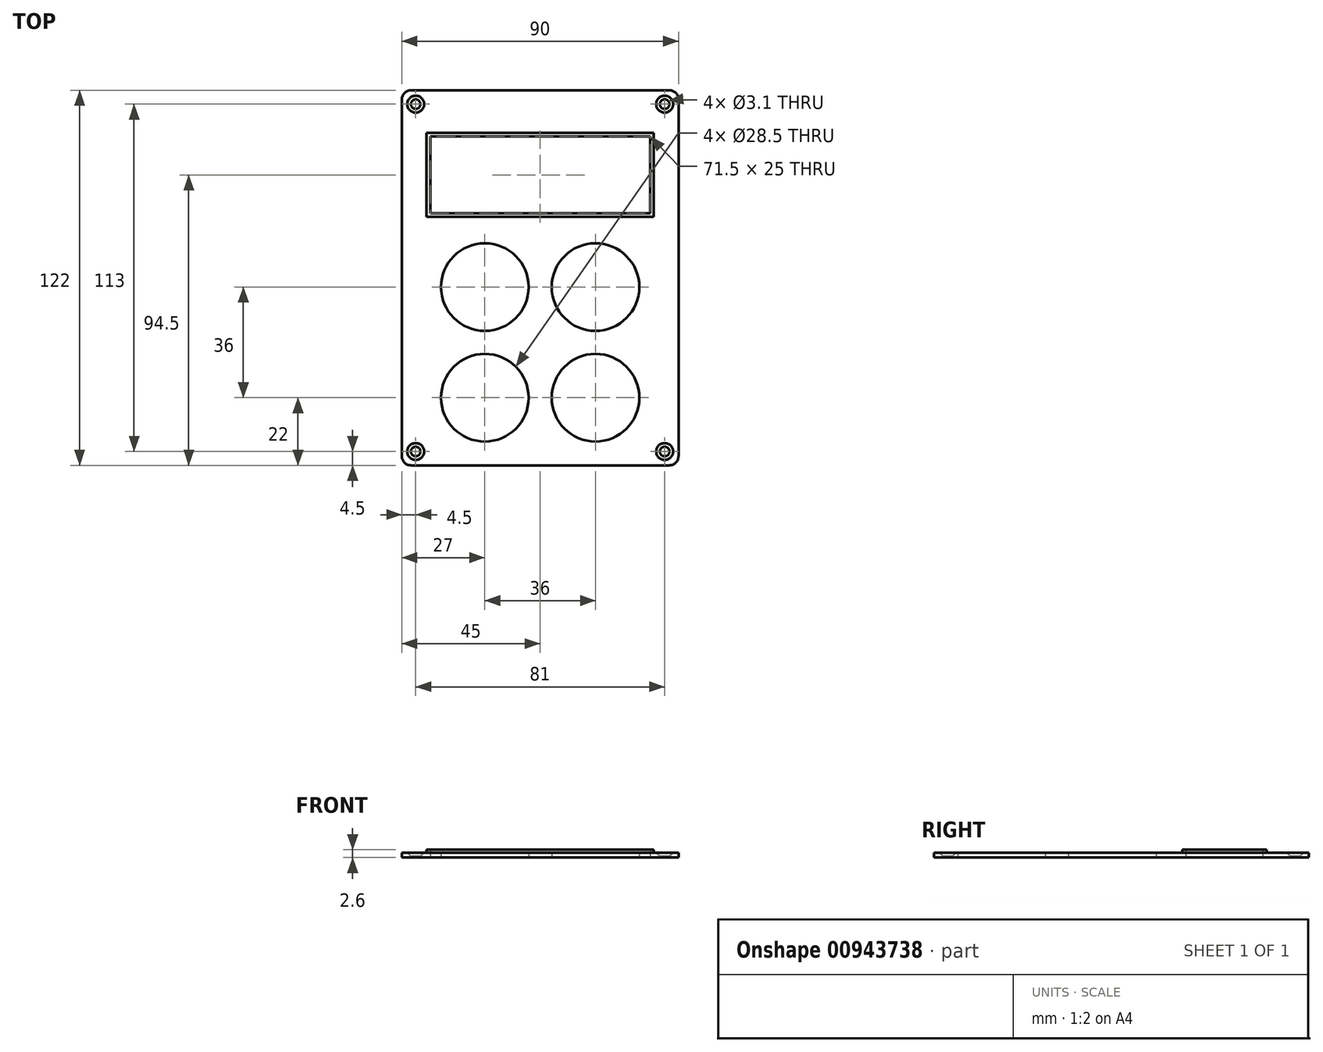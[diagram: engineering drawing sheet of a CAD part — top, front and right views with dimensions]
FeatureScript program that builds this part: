
annotation { "Feature Type Name" : "Feature", "Feature Type Description" : "" }
export const myFeature = defineFeature(function(context is Context, id is Id, definition is map)
    precondition{}
    {
        {
            var Q0;
            Q0=qCreatedBy(makeId("Top.planeOp"),FACE);
            var sketch = newSketch(context, id + "F0", { "sketchPlane" : qUnion([Q0])});
            skLineSegment(sketch, "E0.bottom", {"start": v(42, -94.5) * mm, "end": v(-42, -94.5) * mm});
            skLineSegment(sketch, "E0.top", {"start": v(42, 27.5) * mm, "end": v(-42, 27.5) * mm});
            skLineSegment(sketch, "E0.left", {"start": v(45, -91.5) * mm, "end": v(45, 24.5) * mm});
            skLineSegment(sketch, "E0.right", {"start": v(-45, -91.5) * mm, "end": v(-45, 24.5) * mm});
            skCircle(sketch, "E1", {"center": v(-40.5, -90) * mm, "radius": 1.55 * mm});
            skCircle(sketch, "E2", {"center": v(40.5, 23) * mm, "radius": 1.55 * mm});
            skCircle(sketch, "E3", {"center": v(40.5, -90) * mm, "radius": 1.55 * mm});
            skLineSegment(sketch, "E4.bottom", {"start": v(35.75, -12.5) * mm, "end": v(-35.75, -12.5) * mm});
            skLineSegment(sketch, "E4.top", {"start": v(35.75, 12.5) * mm, "end": v(-35.75, 12.5) * mm});
            skLineSegment(sketch, "E4.left", {"start": v(35.75, -12.5) * mm, "end": v(35.75, 12.5) * mm});
            skLineSegment(sketch, "E4.right", {"start": v(-35.75, -12.5) * mm, "end": v(-35.75, 12.5) * mm});
            skPoint(sketch, "E4.middle", {"position": v(0, 0) * mm});
            skPoint(sketch, "E5", {"position": v(0, 27.5) * mm});
            skCircle(sketch, "E6", {"center": v(-18, -36.5) * mm, "radius": 14.25 * mm});
            skCircle(sketch, "E7", {"center": v(18, -36.5) * mm, "radius": 14.25 * mm});
            skCircle(sketch, "E8", {"center": v(-18, -72.5) * mm, "radius": 14.25 * mm});
            skCircle(sketch, "E9", {"center": v(18, -72.5) * mm, "radius": 14.25 * mm});
            skPoint(sketch, "E10.visualSharp", {"position": v(45, 27.5) * mm});
            skArc(sketch, "E10.filletArc", {"start": v(45, 24.5) * mm, "mid": v(44.12, 26.62) * mm, "end": v(42, 27.5) * mm});
            skPoint(sketch, "E11.visualSharp", {"position": v(-45, 27.5) * mm});
            skArc(sketch, "E11.filletArc", {"start": v(-42, 27.5) * mm, "mid": v(-44.12, 26.62) * mm, "end": v(-45, 24.5) * mm});
            skPoint(sketch, "E12.visualSharp", {"position": v(-45, -94.5) * mm});
            skArc(sketch, "E12.filletArc", {"start": v(-45, -91.5) * mm, "mid": v(-44.12, -93.62) * mm, "end": v(-42, -94.5) * mm});
            skPoint(sketch, "E13.visualSharp", {"position": v(45, -94.5) * mm});
            skArc(sketch, "E13.filletArc", {"start": v(42, -94.5) * mm, "mid": v(44.12, -93.62) * mm, "end": v(45, -91.5) * mm});
            skCircle(sketch, "E14", {"center": v(-40.5, 23) * mm, "radius": 1.55 * mm});
            skSolve(sketch);
        }
        {
            var Q0;
            Q0=qSketchRegion(id+"F0",true);
            extrude(context, id + "F1", {"entities" : qUnion([Q0]), "depth" : 1.6 * mm, "offsetDistance" : 25 * mm});
        }
        {
            var Q0;
            {var subQ0=sQuery(id+"F0.wireOp",EDGE,"E12.filletArc");var subQ1=sQuery(id+"F0.wireOp",EDGE,"E11.filletArc");var subQ2=sQuery(id+"F0.wireOp",EDGE,"E9");var subQ3=sQuery(id+"F0.wireOp",EDGE,"E8");var subQ4=sQuery(id+"F0.wireOp",EDGE,"E7");var subQ5=sQuery(id+"F0.wireOp",EDGE,"E6");var subQ6=sQuery(id+"F0.wireOp",EDGE,"E4.right");var subQ7=sQuery(id+"F0.wireOp",EDGE,"E4.left");var subQ8=sQuery(id+"F0.wireOp",EDGE,"E10.filletArc");var subQ9=sQuery(id+"F0.wireOp",EDGE,"E0.left");var subQ10=sQuery(id+"F0.wireOp",EDGE,"E0.top");var subQ11=sQuery(id+"F0.wireOp",EDGE,"E0.right");var subQ12=sQuery(id+"F0.wireOp",EDGE,"E0.bottom");var subQ13=sQuery(id+"F0.wireOp",EDGE,"E4.top");var subQ14=sQuery(id+"F0.wireOp",EDGE,"E1");var subQ15=sQuery(id+"F0.wireOp",EDGE,"E13.filletArc");var subQ16=sQuery(id+"F0.wireOp",EDGE,"16f8IFU0-oIQh-cnNS-k59y-e92YAkWsYWvI");var subQ17=sQuery(id+"F0.wireOp",EDGE,"E2");var subQ18=sQuery(id+"F0.wireOp",EDGE,"E3");var subQ19=sQuery(id+"F0.wireOp",EDGE,"E4.bottom");Q0=makeQuery(id+"FyvMRoPhiwxUSnX_1.boolean.opBoolean","SPLIT",FACE,{"disambiguationData":[TD([makeQuery(id+"F1.opExtrude","SWEPT_FACE",FACE,{"disambiguationData":[OSD([subQ12])]})])],"derivedFrom":makeQuery(id+"F1.opExtrude","CAP_FACE",FACE,{"disambiguationData":[OSD([subQ12,subQ10,subQ9,subQ11,subQ14,subQ16,subQ17,subQ18,subQ19,subQ13,subQ7,subQ6,subQ5,subQ4,subQ3,subQ2,subQ8,subQ1,subQ0,subQ15])],"isStart":false})});}
            var sketch = newSketch(context, id + "F2", { "sketchPlane" : qUnion([Q0])});
            skLineSegment(sketch, "E15.0", {"start": v(36.95, 13.7) * mm, "end": v(-36.95, 13.7) * mm});
            skLineSegment(sketch, "E15.1", {"start": v(36.95, -13.7) * mm, "end": v(36.95, 13.7) * mm});
            skLineSegment(sketch, "E15.2", {"start": v(36.95, -13.7) * mm, "end": v(-36.95, -13.7) * mm});
            skLineSegment(sketch, "E15.3", {"start": v(-36.95, -13.7) * mm, "end": v(-36.95, 13.7) * mm});
            skSolve(sketch);
        }
        {
            var Q0;
            Q0=makeQuery(id+"F2.imprint","IMPRINT",FACE,{"disambiguationData":[TD([[makeQuery(id+"F2.imprint","IMPRINT",EDGE,{"derivedFrom":sQuery(id+"F2.wireOp",EDGE,"E15.0")}),1.0]])]});
            extrude(context, id + "F3", {"entities" : qUnion([Q0]), "operationType" : NewBodyOperationType.ADD, "depth" : 1 * mm, "offsetDistance" : 25 * mm});
        }
        {
            var Q0;
            {var subQ0=sQuery(id+"F0.wireOp",EDGE,"E13.filletArc");var subQ1=sQuery(id+"F0.wireOp",EDGE,"E12.filletArc");var subQ2=sQuery(id+"F0.wireOp",EDGE,"E10.filletArc");var subQ3=sQuery(id+"F0.wireOp",EDGE,"E9");var subQ4=sQuery(id+"F0.wireOp",EDGE,"E8");var subQ5=sQuery(id+"F0.wireOp",EDGE,"E7");var subQ6=sQuery(id+"F0.wireOp",EDGE,"E6");var subQ7=sQuery(id+"F0.wireOp",EDGE,"E4.right");var subQ8=sQuery(id+"F0.wireOp",EDGE,"E11.filletArc");var subQ9=sQuery(id+"F0.wireOp",EDGE,"E0.left");var subQ10=sQuery(id+"F0.wireOp",EDGE,"E0.top");var subQ11=sQuery(id+"F0.wireOp",EDGE,"E0.right");var subQ12=sQuery(id+"F0.wireOp",EDGE,"E0.bottom");var subQ13=sQuery(id+"F0.wireOp",EDGE,"E4.left");var subQ14=sQuery(id+"F0.wireOp",EDGE,"E1");var subQ15=sQuery(id+"F0.wireOp",EDGE,"E14");var subQ16=sQuery(id+"F0.wireOp",EDGE,"E2");var subQ17=sQuery(id+"F0.wireOp",EDGE,"E3");var subQ18=sQuery(id+"F0.wireOp",EDGE,"E4.bottom");var subQ19=sQuery(id+"F0.wireOp",EDGE,"E4.top");Q0=makeQuery(id+"FyvMRoPhiwxUSnX_1.boolean.opBoolean","SPLIT",FACE,{"disambiguationData":[TD([makeQuery(id+"F1.opExtrude","SWEPT_FACE",FACE,{"disambiguationData":[OSD([subQ12])]})])],"derivedFrom":makeQuery(id+"F1.opExtrude","CAP_FACE",FACE,{"disambiguationData":[OSD([subQ12,subQ10,subQ9,subQ11,subQ14,subQ16,subQ17,subQ18,subQ19,subQ13,subQ7,subQ6,subQ5,subQ4,subQ3,subQ2,subQ8,subQ1,subQ0,subQ15])],"isStart":false})});}
            var sketch = newSketch(context, id + "F4", { "sketchPlane" : qUnion([Q0])});
            skPoint(sketch, "E16", {"position": v(-40.5, 23) * mm});
            skPoint(sketch, "E17", {"position": v(40.5, 23) * mm});
            skPoint(sketch, "E18", {"position": v(40.5, -90) * mm});
            skPoint(sketch, "E19", {"position": v(-40.5, -90) * mm});
            skSolve(sketch);
        }
        {
            var Q0;
            Q0=sQuery(id+"F4.wireOp",VERTEX,"E16");
            var Q1;
            Q1=sQuery(id+"F4.wireOp",VERTEX,"E17");
            var Q2;
            Q2=sQuery(id+"F4.wireOp",VERTEX,"E19");
            var Q3;
            Q3=sQuery(id+"F4.wireOp",VERTEX,"E18");
            var Q4;
            Q4=makeQuery(id+"F1.opExtrude","SWEPT_BODY",BODY,{"disambiguationData":[OSD([sQuery(id+"F0.wireOp",EDGE,"E0.bottom"),sQuery(id+"F0.wireOp",EDGE,"E0.top"),sQuery(id+"F0.wireOp",EDGE,"E0.left"),sQuery(id+"F0.wireOp",EDGE,"E0.right"),sQuery(id+"F0.wireOp",EDGE,"E1"),sQuery(id+"F0.wireOp",EDGE,"E2"),sQuery(id+"F0.wireOp",EDGE,"E3"),sQuery(id+"F0.wireOp",EDGE,"E4.bottom"),sQuery(id+"F0.wireOp",EDGE,"E4.top"),sQuery(id+"F0.wireOp",EDGE,"E4.left"),sQuery(id+"F0.wireOp",EDGE,"E4.right"),sQuery(id+"F0.wireOp",EDGE,"E6"),sQuery(id+"F0.wireOp",EDGE,"E7"),sQuery(id+"F0.wireOp",EDGE,"E8"),sQuery(id+"F0.wireOp",EDGE,"E9"),sQuery(id+"F0.wireOp",EDGE,"E10.filletArc"),sQuery(id+"F0.wireOp",EDGE,"E11.filletArc"),sQuery(id+"F0.wireOp",EDGE,"E12.filletArc"),sQuery(id+"F0.wireOp",EDGE,"E13.filletArc"),sQuery(id+"F0.wireOp",EDGE,"E14")])]});
            hole(context, id + "F5", {"style" : HoleStyle.C_SINK, "endStyle" : HoleEndStyle.THROUGH, "holeDiameter" : 3.1 * mm, "cSinkDiameter" : 5.5 * mm, "cSinkAngle" : 90 * degree, "majorDiameter" : 5 * mm, "isTappedThrough" : true, "tappedDepth" : 12 * mm, "tapClearance" : 3, "locations" : qUnion([Q0, Q1, Q2, Q3]), "scope" : qUnion([Q4])});
        }
    });
